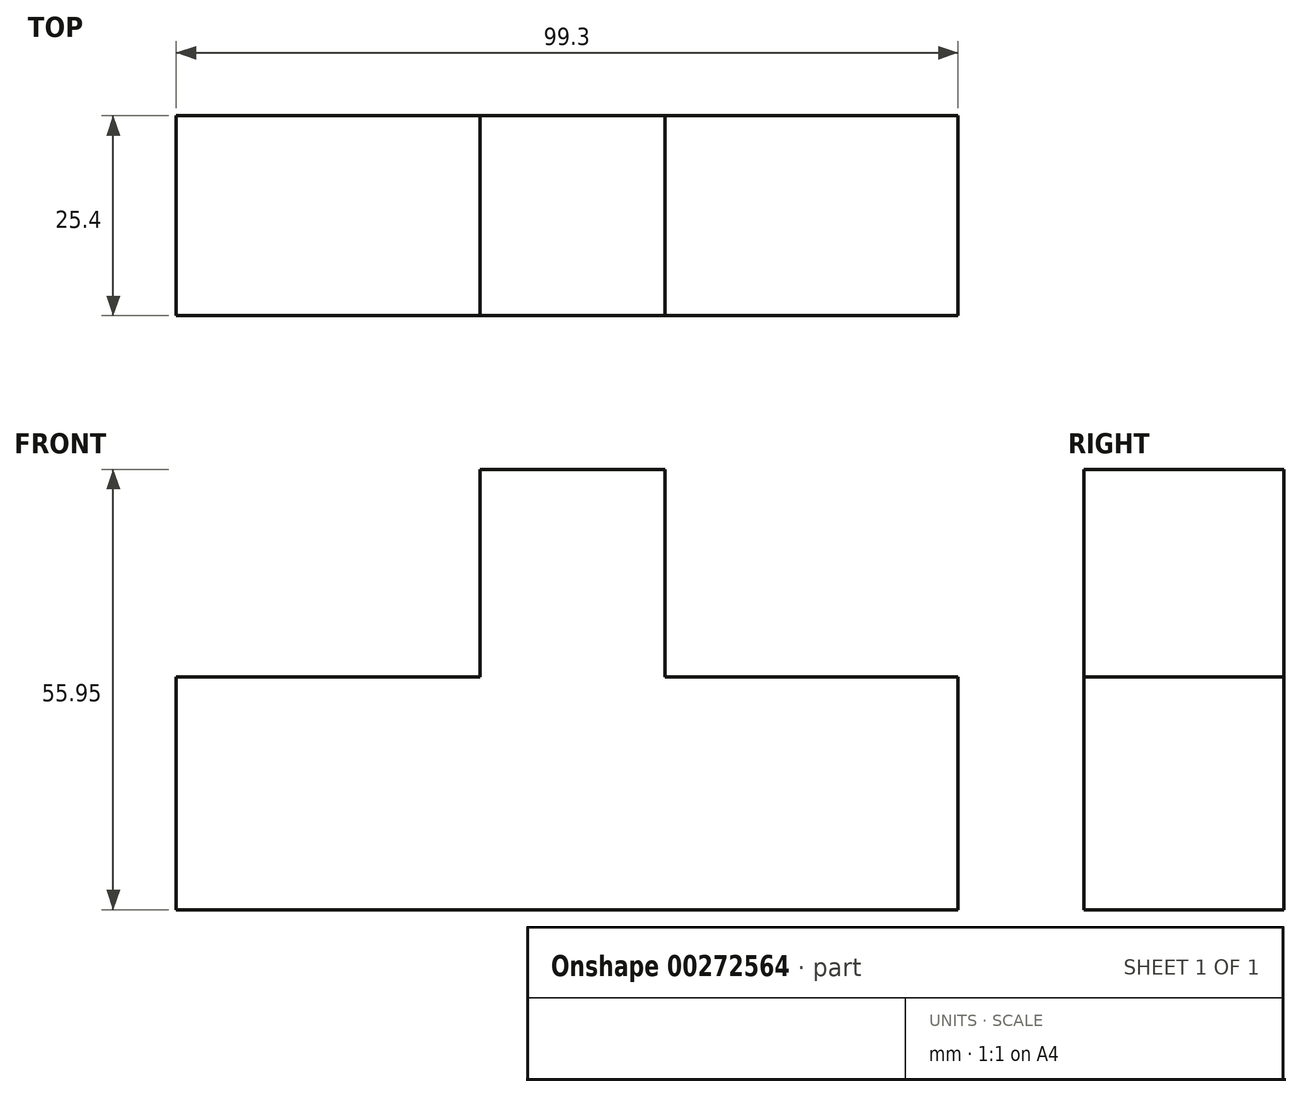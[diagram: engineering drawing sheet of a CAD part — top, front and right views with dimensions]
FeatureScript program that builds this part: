
annotation { "Feature Type Name" : "Feature", "Feature Type Description" : "" }
export const myFeature = defineFeature(function(context is Context, id is Id, definition is map)
    precondition{}
    {
        {
            var Q0;
            Q0=qCreatedBy(makeId("Front.planeOp"),FACE);
            var sketch = newSketch(context, id + "F0", { "sketchPlane" : qUnion([Q0])});
            skLineSegment(sketch, "E0", {"start": v(0, 0) * mm, "end": v(-51.56, 0) * mm});
            skLineSegment(sketch, "E1", {"start": v(-51.56, 0) * mm, "end": v(-51.56, 29.6) * mm});
            skLineSegment(sketch, "E2", {"start": v(-51.56, 29.6) * mm, "end": v(-12.98, 29.6) * mm});
            skLineSegment(sketch, "E3", {"start": v(-12.98, 29.6) * mm, "end": v(-12.98, 55.95) * mm});
            skLineSegment(sketch, "E4", {"start": v(-12.98, 55.95) * mm, "end": v(10.5, 55.95) * mm});
            skLineSegment(sketch, "E5", {"start": v(10.5, 55.95) * mm, "end": v(10.5, 29.6) * mm});
            skLineSegment(sketch, "E6", {"start": v(10.5, 29.6) * mm, "end": v(47.74, 29.6) * mm});
            skLineSegment(sketch, "E7", {"start": v(47.74, 29.6) * mm, "end": v(47.74, 0) * mm});
            skLineSegment(sketch, "E8", {"start": v(47.74, 0) * mm, "end": v(0, 0) * mm});
            skSolve(sketch);
        }
        {
            var Q0;
            Q0 = qSketchRegion(id + "F0", true);
            extrude(context, id + "F1", {"entities" : qUnion([Q0]), "depth" : 25.4 * mm});
        }
    });
